# Revit family: Plumbing-Flushometer-Sloan-Valve-BPW-1100
name_source: partatom
category: Plumbing Fixtures
units: mm (PartAtom-declared; Revit-internal decimal feet)

## family parameters
Cut with Voids When Loaded = No
Host = Face
OmniClass Number = 23.45.05.14.99
Part Type = Normal
Room Calculation Point = No
Round Connector Dimension = Use Diameter
Shared = No

## types (1)
- Not a Type - Load Type Catalog!
    Assembly Code = D2020300
    CW Connection = Yes
    CWFU = 0
    Centerline of Supply from Top of Fixture = 26 1/2"
    Centerline of Supply to Centerline of Valve = 5"
    Default Elevation = 0"
    Description = 1.6 gpf, Polished Chrome Finish, Fixture Connection Top Spud, Single Flush, Front of Valve Handle, Royal® Exposed Manual Specialty Service Sink Bedpan Washer Flushometer.
    Edition number = 1
    Flush Rate = 1.6 gpf (6.0 Lpf)
    HW Connection = No
    HWFU = 0
    Height = 28 1/2"
    Keynote = 15410
    Manufacturer = Sloan Valve
    Model = Model not specified - Load type catalog!
    Operating Water Pressure = 15 – 80 PSI (103 – 552 kPa)
    Part Number = 3019647
    Product Material = Sloan Valve - Finish - Polished Chrome
    URL = www.sloanvalve.com
    Valve Pressure Drop = 0.00 psi
    Vent Connection = No
    WFU = 0
    Waste Connection = No
    Water Inlet Connection Description = Water Inlet Connection
    Water Inlet Connection Diameter = 1"
    z_2D_1 = Yes
    z_Distance = 2 1/2"
    z_Front Handle = Yes
    z_No OFST = Yes
    z_OFST = No
    z_Offset = 2 1/2"
    z_Offset Group 1 = 0"
    z_Pipe Offset = 1"
    z_Side Handle = No
    z_cut offset = 3 1/2"

## geometry (parser evidence)
native form markers: Sweep x2
no freeform markers — native parametric forms only
